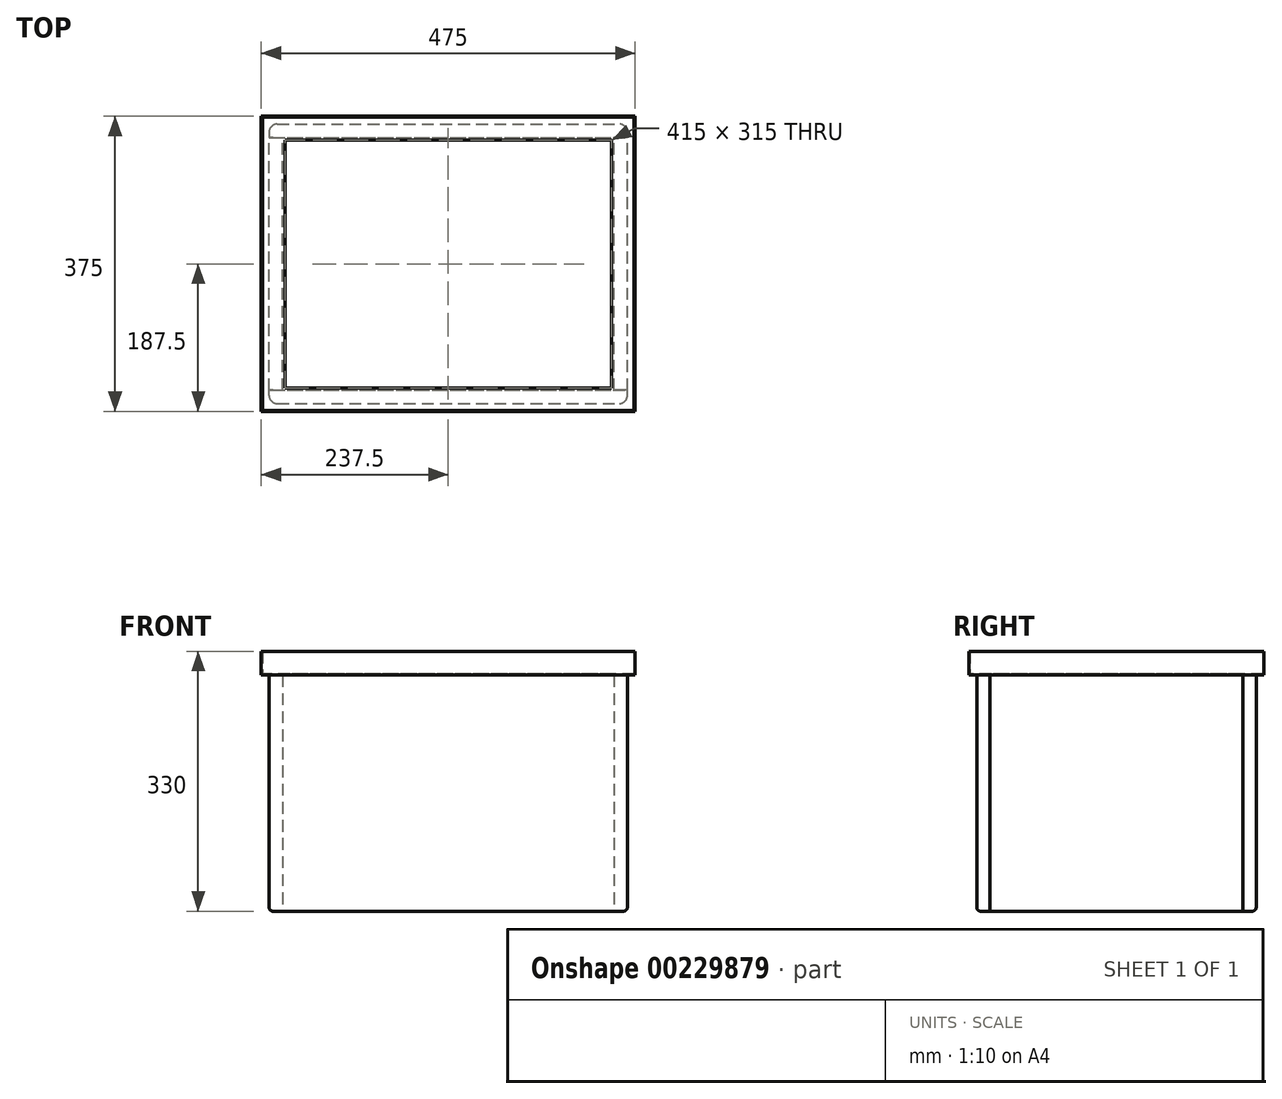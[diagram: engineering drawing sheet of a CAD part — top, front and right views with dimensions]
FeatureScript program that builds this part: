
annotation { "Feature Type Name" : "Feature", "Feature Type Description" : "" }
export const myFeature = defineFeature(function(context is Context, id is Id, definition is map)
    precondition{}
    {
        {
            var Q0;
            Q0=qCreatedBy(makeId("Top.planeOp"),FACE);
            var sketch = newSketch(context, id + "F0", { "sketchPlane" : qUnion([Q0])});
            skLineSegment(sketch, "E0.bottom", {"start": v(-227.5, -177.5) * mm, "end": v(227.5, -177.5) * mm});
            skLineSegment(sketch, "E0.top", {"start": v(-227.5, -160.5) * mm, "end": v(227.5, -160.5) * mm});
            skLineSegment(sketch, "E0.left", {"start": v(-227.5, -177.5) * mm, "end": v(-227.5, -160.5) * mm});
            skLineSegment(sketch, "E0.right", {"start": v(227.5, -177.5) * mm, "end": v(227.5, -160.5) * mm});
            skSolve(sketch);
        }
        {
            var Q0;
            Q0=makeQuery(id+"F0.imprint","IMPRINT",FACE,{"disambiguationData":[TD([[makeQuery(id+"F0.imprint","IMPRINT",EDGE,{"derivedFrom":sQuery(id+"F0.wireOp",EDGE,"E0.bottom")}),1.0]])]});
            extrude(context, id + "F1", {"entities" : qUnion([Q0]), "depth" : 300 * mm});
        }
        {
            var Q0;
            Q0=makeQuery(id+"F1.opExtrude","SWEPT_EDGE",EDGE,{"disambiguationData":[OSD([sQuery(id+"F0.wireOp",EDGE,"E0.bottom"),sQuery(id+"F0.wireOp",EDGE,"E0.left")])]});
            var Q1;
            Q1=makeQuery(id+"F1.opExtrude","SWEPT_EDGE",EDGE,{"disambiguationData":[OSD([sQuery(id+"F0.wireOp",EDGE,"E0.bottom"),sQuery(id+"F0.wireOp",EDGE,"E0.right")])]});
            fillet(context, id + "F2", {"entities" : qUnion([Q0, Q1]), "radius" : 10 * mm, "tangentPropagation" : true, "allowEdgeOverflow" : false});
        }
        {
            var Q0;
            Q0=makeQuery(id+"F1.opExtrude","CAP_EDGE",EDGE,{"disambiguationData":[OSD([sQuery(id+"F0.wireOp",EDGE,"E0.bottom")])],"isStart":true});
            fillet(context, id + "F3", {"entities" : qUnion([Q0]), "radius" : 5 * mm, "tangentPropagation" : true, "allowEdgeOverflow" : false});
        }
        {
            var Q0;
            Q0=qCreatedBy(makeId("Top.planeOp"),FACE);
            var sketch = newSketch(context, id + "F4", { "sketchPlane" : qUnion([Q0])});
            skLineSegment(sketch, "E1.bottom", {"start": v(-227.5, -160.5) * mm, "end": v(-210.5, -160.5) * mm});
            skLineSegment(sketch, "E1.top", {"start": v(-227.5, 160.5) * mm, "end": v(-210.5, 160.5) * mm});
            skLineSegment(sketch, "E1.left", {"start": v(-227.5, -160.5) * mm, "end": v(-227.5, 160.5) * mm});
            skLineSegment(sketch, "E1.right", {"start": v(-210.5, -160.5) * mm, "end": v(-210.5, 160.5) * mm});
            skSolve(sketch);
        }
        {
            var Q0;
            Q0=makeQuery(id+"F4.imprint","IMPRINT",FACE,{"disambiguationData":[TD([[makeQuery(id+"F4.imprint","IMPRINT",EDGE,{"derivedFrom":sQuery(id+"F4.wireOp",EDGE,"E1.bottom")}),1.0]])]});
            extrude(context, id + "F5", {"entities" : qUnion([Q0]), "depth" : 300 * mm});
        }
        {
            var Q0;
            Q0=makeQuery(id+"F5.opExtrude","CAP_EDGE",EDGE,{"disambiguationData":[OSD([sQuery(id+"F4.wireOp",EDGE,"E1.left")])],"isStart":true});
            fillet(context, id + "F6", {"entities" : qUnion([Q0]), "radius" : 5 * mm, "tangentPropagation" : true, "allowEdgeOverflow" : false});
        }
        {
            var Q0;
            Q0=makeQuery(id+"F1.opExtrude","SWEPT_BODY",BODY,{"disambiguationData":[OSD([sQuery(id+"F0.wireOp",EDGE,"E0.bottom"),sQuery(id+"F0.wireOp",EDGE,"E0.top"),sQuery(id+"F0.wireOp",EDGE,"E0.left"),sQuery(id+"F0.wireOp",EDGE,"E0.right")])]});
            var Q1;
            Q1=qCreatedBy(makeId("Front.planeOp"),FACE);
            mirror(context, id + "F7", {"entities" : qUnion([Q0]), "mirrorPlane" : qUnion([Q1])});
        }
        {
            var Q0;
            Q0=makeQuery(id+"F5.opExtrude","SWEPT_BODY",BODY,{"disambiguationData":[OSD([sQuery(id+"F4.wireOp",EDGE,"E1.bottom"),sQuery(id+"F4.wireOp",EDGE,"E1.top"),sQuery(id+"F4.wireOp",EDGE,"E1.left"),sQuery(id+"F4.wireOp",EDGE,"E1.right")])]});
            var Q1;
            Q1=qCreatedBy(makeId("Right.planeOp"),FACE);
            mirror(context, id + "F8", {"entities" : qUnion([Q0]), "mirrorPlane" : qUnion([Q1])});
        }
        {
            var Q0;
            Q0=makeQuery(id+"F5.opExtrude","CAP_FACE",FACE,{"disambiguationData":[OSD([sQuery(id+"F4.wireOp",EDGE,"E1.bottom"),sQuery(id+"F4.wireOp",EDGE,"E1.top"),sQuery(id+"F4.wireOp",EDGE,"E1.left"),sQuery(id+"F4.wireOp",EDGE,"E1.right")])],"isStart":false});
            var sketch = newSketch(context, id + "F9", { "sketchPlane" : qUnion([Q0])});
            skLineSegment(sketch, "E2.bottom", {"start": v(237.5, 187.5) * mm, "end": v(-237.5, 187.5) * mm});
            skLineSegment(sketch, "E2.top", {"start": v(237.5, -187.5) * mm, "end": v(-237.5, -187.5) * mm});
            skLineSegment(sketch, "E2.left", {"start": v(237.5, 187.5) * mm, "end": v(237.5, -187.5) * mm});
            skLineSegment(sketch, "E2.right", {"start": v(-237.5, 187.5) * mm, "end": v(-237.5, -187.5) * mm});
            skPoint(sketch, "E2.middle", {"position": v(0, 0) * mm});
            skLineSegment(sketch, "E3.bottom", {"start": v(207.5, 157.5) * mm, "end": v(-207.5, 157.5) * mm});
            skLineSegment(sketch, "E3.top", {"start": v(207.5, -157.5) * mm, "end": v(-207.5, -157.5) * mm});
            skLineSegment(sketch, "E3.left", {"start": v(207.5, 157.5) * mm, "end": v(207.5, -157.5) * mm});
            skLineSegment(sketch, "E3.right", {"start": v(-207.5, 157.5) * mm, "end": v(-207.5, -157.5) * mm});
            skSolve(sketch);
        }
        {
            var Q0;
            Q0 = qSketchRegion(id + "F9", true);
            extrude(context, id + "F10", {"entities" : qUnion([Q0]), "depth" : 30 * mm});
        }
        {
            var Q0;
            Q0=makeQuery(id+"F10.opExtrude","CAP_FACE",FACE,{"disambiguationData":[OSD([sQuery(id+"F9.wireOp",EDGE,"E2.bottom"),sQuery(id+"F9.wireOp",EDGE,"E2.top"),sQuery(id+"F9.wireOp",EDGE,"E2.left"),sQuery(id+"F9.wireOp",EDGE,"E2.right"),sQuery(id+"F9.wireOp",EDGE,"E3.bottom"),sQuery(id+"F9.wireOp",EDGE,"E3.top"),sQuery(id+"F9.wireOp",EDGE,"E3.left"),sQuery(id+"F9.wireOp",EDGE,"E3.right")])],"isStart":false});
            var Q1;
            Q1=makeQuery(id+"F10.opExtrude","SWEPT_FACE",FACE,{"disambiguationData":[OSD([sQuery(id+"F9.wireOp",EDGE,"E3.bottom")])]});
            var Q2;
            Q2=makeQuery(id+"F10.opExtrude","SWEPT_FACE",FACE,{"disambiguationData":[OSD([sQuery(id+"F9.wireOp",EDGE,"E3.right")])]});
            var Q3;
            Q3=makeQuery(id+"F10.opExtrude","SWEPT_FACE",FACE,{"disambiguationData":[OSD([sQuery(id+"F9.wireOp",EDGE,"E3.left")])]});
            var Q4;
            Q4=makeQuery(id+"F10.opExtrude","SWEPT_FACE",FACE,{"disambiguationData":[OSD([sQuery(id+"F9.wireOp",EDGE,"E3.top")])]});
            shell(context, id + "F11", {"entities" : qUnion([Q0, Q1, Q2, Q3, Q4]), "thickness" : 1.4 * mm});
        }
    });
